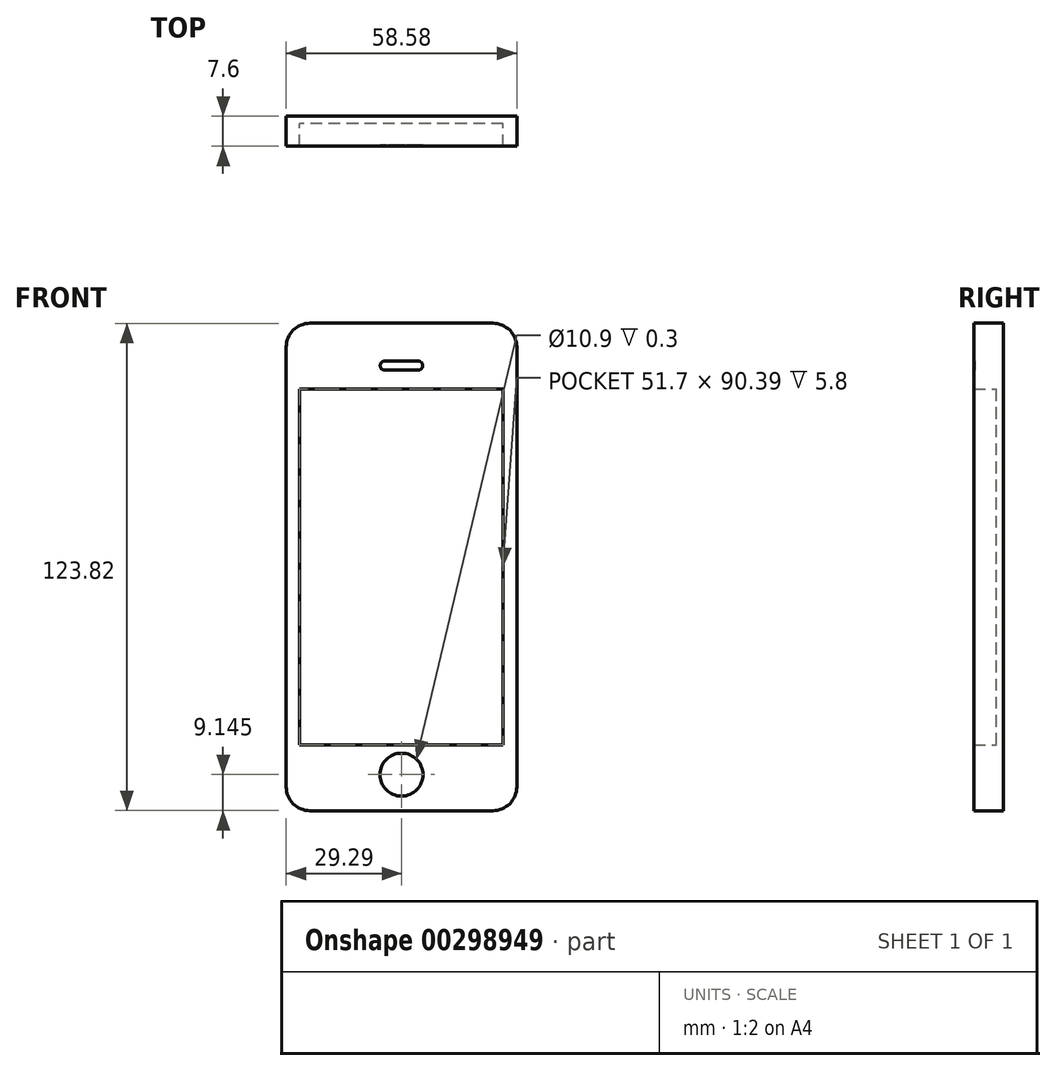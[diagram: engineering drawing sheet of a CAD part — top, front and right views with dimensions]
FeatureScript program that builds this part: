
annotation { "Feature Type Name" : "Feature", "Feature Type Description" : "" }
export const myFeature = defineFeature(function(context is Context, id is Id, definition is map)
    precondition{}
    {
        {
            var Q0;
            Q0=qCreatedBy(makeId("Front.planeOp"),FACE);
            var sketch = newSketch(context, id + "F0", { "sketchPlane" : qUnion([Q0])});
            skLineSegment(sketch, "E0.bottom", {"start": v(29.29, -61.91) * mm, "end": v(-29.28, -61.92) * mm});
            skLineSegment(sketch, "E0.top", {"start": v(29.28, 61.91) * mm, "end": v(-29.29, 61.91) * mm});
            skLineSegment(sketch, "E0.left", {"start": v(29.29, -61.91) * mm, "end": v(29.28, 61.92) * mm});
            skLineSegment(sketch, "E0.right", {"start": v(-29.28, -61.92) * mm, "end": v(-29.29, 61.92) * mm});
            skPoint(sketch, "E0.middle", {"position": v(0, 0) * mm});
            skLineSegment(sketch, "E1.bottom", {"start": v(25.85, -45.2) * mm, "end": v(-25.85, -45.2) * mm});
            skLineSegment(sketch, "E1.top", {"start": v(25.85, 45.2) * mm, "end": v(-25.85, 45.2) * mm});
            skLineSegment(sketch, "E1.left", {"start": v(25.85, -45.2) * mm, "end": v(25.85, 45.2) * mm});
            skLineSegment(sketch, "E1.right", {"start": v(-25.85, -45.2) * mm, "end": v(-25.85, 45.2) * mm});
            skLineSegment(sketch, "E2", {"start": v(0, -61.91) * mm, "end": v(0, -52.77) * mm});
            skCircle(sketch, "E3", {"center": v(0, -52.77) * mm, "radius": 5.45 * mm});
            skLineSegment(sketch, "E4.bottom", {"start": v(5.4, 50.01) * mm, "end": v(-5.4, 50.01) * mm});
            skLineSegment(sketch, "E4.top", {"start": v(5.4, 52.31) * mm, "end": v(-5.4, 52.31) * mm});
            skLineSegment(sketch, "E4.left", {"start": v(5.4, 50.01) * mm, "end": v(5.4, 52.31) * mm});
            skLineSegment(sketch, "E4.right", {"start": v(-5.4, 50.01) * mm, "end": v(-5.4, 52.31) * mm});
            skPoint(sketch, "E4.middle", {"position": v(0, 51.16) * mm});
            skSolve(sketch);
        }
        {
            var Q0;
            Q0=makeQuery(id+"F0.imprint","IMPRINT",FACE,{"disambiguationData":[TD([[makeQuery(id+"F0.imprint","IMPRINT",EDGE,{"derivedFrom":sQuery(id+"F0.wireOp",EDGE,"E0.bottom")}),-1.0]])]});
            extrude(context, id + "F1", {"entities" : qUnion([Q0]), "depth" : 7.6 * mm});
        }
        {
            var Q0;
            Q0=makeQuery(id+"F1.opExtrude","SWEPT_EDGE",EDGE,{"disambiguationData":[OSD([sQuery(id+"F0.wireOp",EDGE,"E0.top"),sQuery(id+"F0.wireOp",EDGE,"E0.right")])]});
            var Q1;
            Q1=makeQuery(id+"F1.opExtrude","SWEPT_EDGE",EDGE,{"disambiguationData":[OSD([sQuery(id+"F0.wireOp",EDGE,"E0.top"),sQuery(id+"F0.wireOp",EDGE,"E0.left")])]});
            var Q2;
            Q2=makeQuery(id+"F1.opExtrude","SWEPT_EDGE",EDGE,{"disambiguationData":[OSD([sQuery(id+"F0.wireOp",EDGE,"E0.bottom"),sQuery(id+"F0.wireOp",EDGE,"E0.right")])]});
            var Q3;
            Q3=makeQuery(id+"F1.opExtrude","SWEPT_EDGE",EDGE,{"disambiguationData":[OSD([sQuery(id+"F0.wireOp",EDGE,"E0.bottom"),sQuery(id+"F0.wireOp",EDGE,"E0.left")])]});
            fillet(context, id + "F2", {"entities" : qUnion([Q0, Q1, Q2, Q3]), "radius" : 6.07 * mm, "tangentPropagation" : true, "allowEdgeOverflow" : false});
        }
        {
            var Q0;
            Q0=makeQuery(id+"F0.imprint","IMPRINT",FACE,{"disambiguationData":[TD([[makeQuery(id+"F0.imprint","IMPRINT",EDGE,{"derivedFrom":sQuery(id+"F0.wireOp",EDGE,"E1.bottom")}),-1.0]])]});
            extrude(context, id + "F3", {"entities" : qUnion([Q0]), "operationType" : NewBodyOperationType.ADD, "depth" : 1.8 * mm});
        }
        {
            var Q0;
            Q0=makeQuery(id+"F1.opExtrude","SWEPT_EDGE",EDGE,{"disambiguationData":[OSD([sQuery(id+"F0.wireOp",EDGE,"E4.top"),sQuery(id+"F0.wireOp",EDGE,"E4.right")])]});
            var Q1;
            Q1=makeQuery(id+"F1.opExtrude","SWEPT_EDGE",EDGE,{"disambiguationData":[OSD([sQuery(id+"F0.wireOp",EDGE,"E4.top"),sQuery(id+"F0.wireOp",EDGE,"E4.left")])]});
            var Q2;
            Q2=makeQuery(id+"F1.opExtrude","SWEPT_EDGE",EDGE,{"disambiguationData":[OSD([sQuery(id+"F0.wireOp",EDGE,"E4.bottom"),sQuery(id+"F0.wireOp",EDGE,"E4.left")])]});
            var Q3;
            Q3=makeQuery(id+"F1.opExtrude","SWEPT_EDGE",EDGE,{"disambiguationData":[OSD([sQuery(id+"F0.wireOp",EDGE,"E4.bottom"),sQuery(id+"F0.wireOp",EDGE,"E4.right")])]});
            fillet(context, id + "F4", {"entities" : qUnion([Q0, Q1, Q2, Q3]), "radius" : 1.15 * mm, "tangentPropagation" : true, "allowEdgeOverflow" : false});
        }
        {
            var Q0;
            Q0=makeQuery(id+"F0.imprint","IMPRINT",FACE,{"disambiguationData":[TD([[makeQuery(id+"F0.imprint","IMPRINT",EDGE,{"derivedFrom":sQuery(id+"F0.wireOp",EDGE,"E4.bottom")}),-1.0]])]});
            extrude(context, id + "F5", {"entities" : qUnion([Q0]), "operationType" : NewBodyOperationType.ADD, "depth" : 7.3 * mm});
        }
        {
            var Q0;
            Q0=makeQuery(id+"F0.imprint","IMPRINT",FACE,{"disambiguationData":[TD([[makeQuery(id+"F0.imprint","IMPRINT",EDGE,{"derivedFrom":sQuery(id+"F0.wireOp",EDGE,"E3")}),1.0]])]});
            var Q1;
            Q1=sQuery(id+"F0.wireOp",EDGE,"E3");
            extrude(context, id + "F6", {"entities" : qUnion([Q0]), "operationType" : NewBodyOperationType.ADD, "surfaceEntities" : qUnion([Q1]), "depth" : 7.3 * mm});
        }
    });
